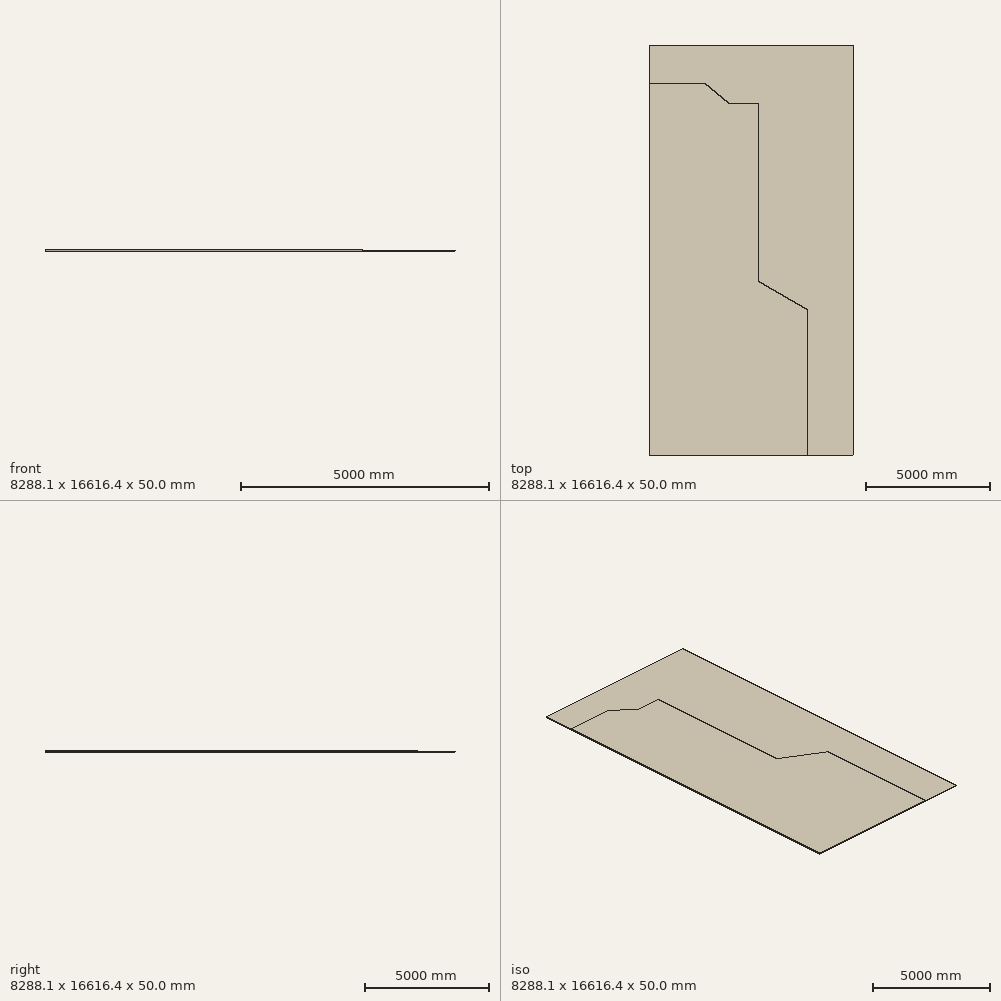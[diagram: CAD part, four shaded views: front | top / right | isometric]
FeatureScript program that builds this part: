
annotation { "Feature Type Name" : "Feature", "Feature Type Description" : "" }
export const myFeature = defineFeature(function(context is Context, id is Id, definition is map)
    precondition{}
    {
        {
            var Q0;
            Q0=qCreatedBy(makeId("Top.planeOp"),FACE);
            var sketch = newSketch(context, id + "F0", { "sketchPlane" : qUnion([Q0])});
            skLineSegment(sketch, "E0", {"start": v(-2250, 2435.62) * mm, "end": v(0, 2435.62) * mm});
            skLineSegment(sketch, "E1", {"start": v(0, 2435.62) * mm, "end": v(995.86, 1600) * mm});
            skLineSegment(sketch, "E2", {"start": v(995.86, 1600) * mm, "end": v(2195.86, 1600) * mm});
            skLineSegment(sketch, "E3", {"start": v(2195.86, 1600) * mm, "end": v(2195.86, 600) * mm});
            skLineSegment(sketch, "E4", {"start": v(2195.86, 600) * mm, "end": v(2195.86, 0) * mm});
            skLineSegment(sketch, "E5", {"start": v(2195.86, 0) * mm, "end": v(2195.86, -5610) * mm});
            skLineSegment(sketch, "E6", {"start": v(2195.86, -5610) * mm, "end": v(4161.74, -6745) * mm});
            skLineSegment(sketch, "E7", {"start": v(4161.74, -6745) * mm, "end": v(4161.74, -12655) * mm});
            skLineSegment(sketch, "E8.bottom", {"start": v(-2250, 3961.38) * mm, "end": v(6038.06, 3961.38) * mm});
            skLineSegment(sketch, "E8.top", {"start": v(-2250, -12655) * mm, "end": v(6038.06, -12655) * mm});
            skLineSegment(sketch, "E8.left", {"start": v(-2250, 3961.38) * mm, "end": v(-2250, -12655) * mm});
            skLineSegment(sketch, "E8.right", {"start": v(6038.06, 3961.38) * mm, "end": v(6038.06, -12655) * mm});
            skSolve(sketch);
        }
        {
            var Q0;
            Q0=sQuery(id+"F0.wireOp",EDGE,"E0");
            var Q1;
            Q1=sQuery(id+"F0.wireOp",EDGE,"E1");
            var Q2;
            Q2=sQuery(id+"F0.wireOp",EDGE,"E2");
            var Q3;
            Q3=sQuery(id+"F0.wireOp",EDGE,"E3");
            var Q4;
            Q4=sQuery(id+"F0.wireOp",EDGE,"E5");
            var Q5;
            Q5=sQuery(id+"F0.wireOp",EDGE,"E6");
            var Q6;
            Q6=sQuery(id+"F0.wireOp",EDGE,"E7");
            extrude(context, id + "F1", {"bodyType" : ToolBodyType.SURFACE, "surfaceEntities" : qUnion([Q0, Q1, Q2, Q3, Q4, Q5, Q6]), "depth" : 1000 * mm, "offsetDistance" : 25 * mm});
        }
        {
            var Q0;
            Q0=sQuery(id+"F0.wireOp",EDGE,"E4");
            extrude(context, id + "F2", {"bodyType" : ToolBodyType.SURFACE, "surfaceEntities" : qUnion([Q0]), "depth" : 1000 * mm, "offsetDistance" : 25 * mm});
        }
        {
            var Q0;
            Q0 = qSketchRegion(id + "F0", true);
            extrude(context, id + "F3", {"entities" : qUnion([Q0]), "oppositeDirection" : true, "depth" : 25 * mm, "offsetDistance" : 25 * mm});
        }
        {
            var Q0;
            Q0=sQuery(id+"F0.wireOp",EDGE,"E8.left");
            var Q1;
            Q1=sQuery(id+"F0.wireOp",EDGE,"E8.top");
            extrude(context, id + "F4", {"bodyType" : ToolBodyType.SURFACE, "surfaceEntities" : qUnion([Q0, Q1]), "depth" : 3000 * mm, "offsetDistance" : 25 * mm});
        }
        {
            var Q0;
            {var subQ1=sQuery(id+"F0.wireOp",EDGE,"E0");Q0=makeQuery(id+"F0.imprint","IMPRINT",FACE,{"disambiguationData":[TD([[makeQuery(id+"F0.imprint","IMPRINT",EDGE,{"derivedFrom":subQ1}),-1.0]])]});}
            extrude(context, id + "F5", {"entities" : qUnion([Q0]), "operationType" : NewBodyOperationType.ADD, "depth" : 25 * mm, "offsetDistance" : 25 * mm});
        }
    });
